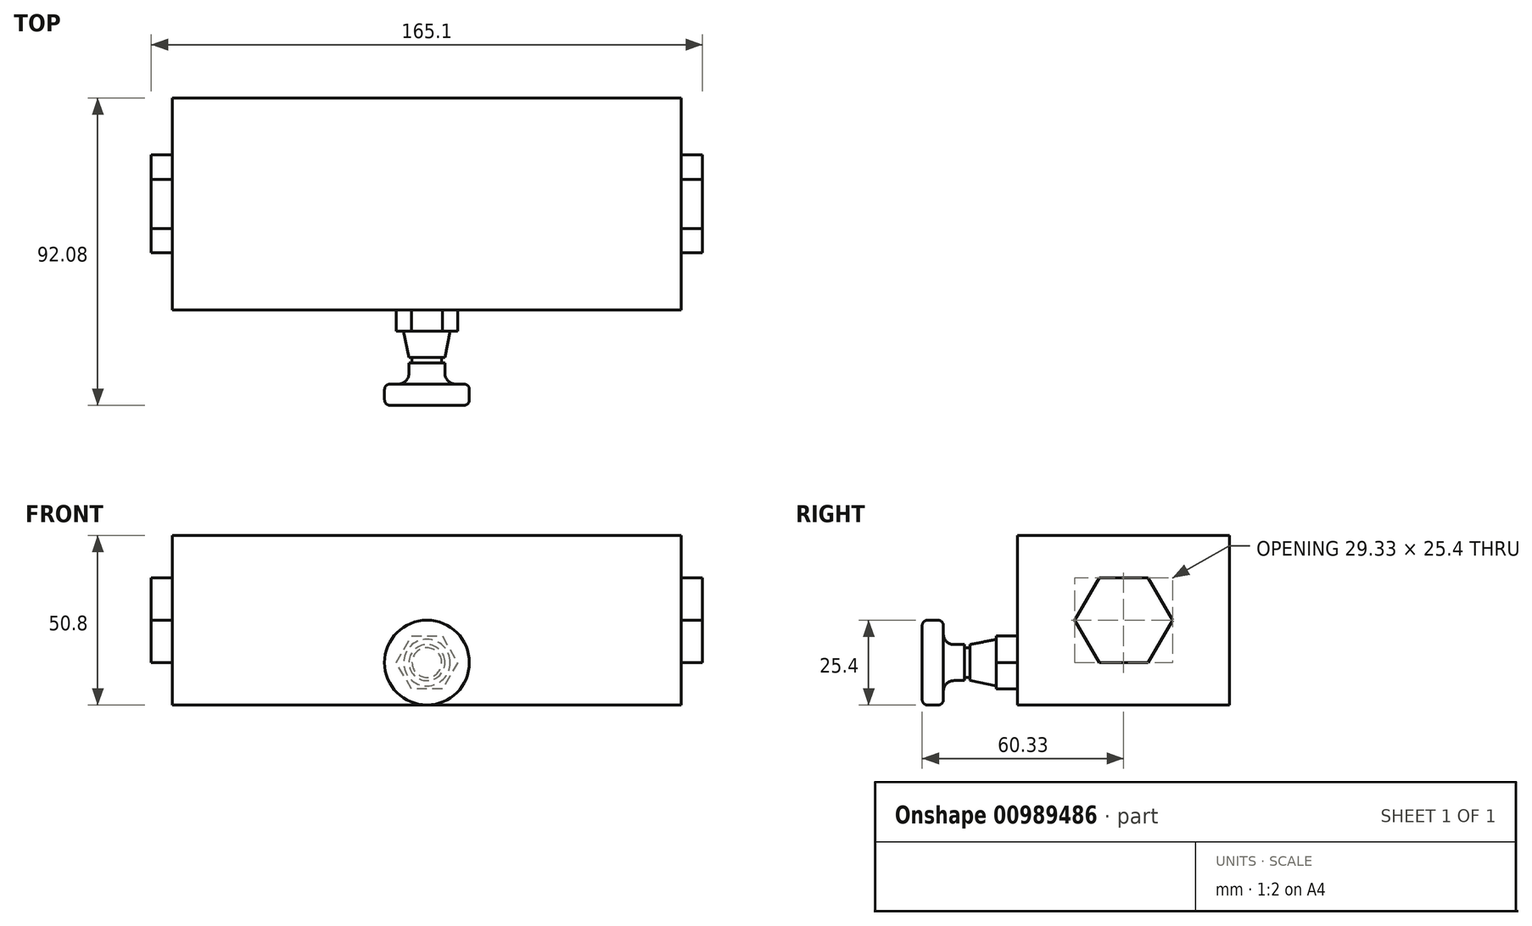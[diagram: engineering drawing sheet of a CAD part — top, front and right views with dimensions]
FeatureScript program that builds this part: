
annotation { "Feature Type Name" : "Feature", "Feature Type Description" : "" }
export const myFeature = defineFeature(function(context is Context, id is Id, definition is map)
    precondition{}
    {
        {
            var Q0;
            Q0=qCreatedBy(makeId("Right.planeOp"),FACE);
            var sketch = newSketch(context, id + "F0", { "sketchPlane" : qUnion([Q0])});
            skLineSegment(sketch, "E0.bottom", {"start": v(31.75, 25.4) * mm, "end": v(-31.75, 25.4) * mm});
            skLineSegment(sketch, "E0.top", {"start": v(31.75, -25.4) * mm, "end": v(-31.75, -25.4) * mm});
            skLineSegment(sketch, "E0.left", {"start": v(31.75, 25.4) * mm, "end": v(31.75, -25.4) * mm});
            skLineSegment(sketch, "E0.right", {"start": v(-31.75, 25.4) * mm, "end": v(-31.75, -25.4) * mm});
            skPoint(sketch, "E0.middle", {"position": v(0, 0) * mm});
            skSolve(sketch);
        }
        {
            var Q0;
            Q0 = qSketchRegion(id + "F0", true);
            extrude(context, id + "F1", {"entities" : qUnion([Q0]), "depth" : 76.2 * mm, "offsetDistance" : 25.4 * mm, "hasSecondDirection" : true, "secondDirectionOppositeDirection" : true, "secondDirectionDepth" : 76.2 * mm});
        }
        {
            var Q0;
            Q0=makeQuery(id+"F1.opExtrude","CAP_FACE",FACE,{"disambiguationData":[OSD([sQuery(id+"F0.wireOp",EDGE,"E0.bottom"),sQuery(id+"F0.wireOp",EDGE,"E0.top"),sQuery(id+"F0.wireOp",EDGE,"E0.left"),sQuery(id+"F0.wireOp",EDGE,"E0.right")])],"isStart":true});
            var sketch = newSketch(context, id + "F2", { "sketchPlane" : qUnion([Q0])});
            skCircle(sketch, "E1.cCircle", {"center": v(0, 0) * mm, "radius": 12.7 * mm, "construction": true});
            skPoint(sketch, "E1.cCircle.centerSnap0", {"position": v(0, 25.4) * mm});
            skPoint(sketch, "E1.cCircle.centerSnap1", {"position": v(31.75, 0) * mm});
            skLineSegment(sketch, "E1.0", {"start": v(-7.33, 12.7) * mm, "end": v(7.33, 12.7) * mm});
            skLineSegment(sketch, "E1.1", {"start": v(7.33, 12.7) * mm, "end": v(14.66, 0) * mm});
            skLineSegment(sketch, "E1.2", {"start": v(14.66, 0) * mm, "end": v(7.33, -12.7) * mm});
            skLineSegment(sketch, "E1.3", {"start": v(7.33, -12.7) * mm, "end": v(-7.33, -12.7) * mm});
            skLineSegment(sketch, "E1.4", {"start": v(-7.33, -12.7) * mm, "end": v(-14.66, 0) * mm});
            skLineSegment(sketch, "E1.5", {"start": v(-14.66, 0) * mm, "end": v(-7.33, 12.7) * mm});
            skPoint(sketch, "E1.0.midPoint", {"position": v(0, 12.7) * mm});
            skSolve(sketch);
        }
        {
            var Q0;
            Q0 = qSketchRegion(id + "F2", true);
            extrude(context, id + "F3", {"entities" : qUnion([Q0]), "operationType" : NewBodyOperationType.ADD, "depth" : 6.35 * mm, "offsetDistance" : 25.4 * mm});
        }
        {
            var Q0;
            Q0=qCreatedBy(makeId("Front.planeOp"),FACE);
            var sketch = newSketch(context, id + "F4", { "sketchPlane" : qUnion([Q0])});
            skLineSegment(sketch, "E2.0", {"start": v(-82.55, 12.7) * mm, "end": v(-82.55, 0) * mm, "construction": true});
            skLineSegment(sketch, "E3.0", {"start": v(-82.55, 0) * mm, "end": v(-82.55, -12.7) * mm, "construction": true});
            skLineSegment(sketch, "E4", {"start": v(-82.55, 11.11) * mm, "end": v(-98.42, 7.94) * mm});
            skLineSegment(sketch, "E5", {"start": v(-98.42, 7.94) * mm, "end": v(-98.42, 6.35) * mm});
            skLineSegment(sketch, "E6", {"start": v(-98.42, 6.35) * mm, "end": v(-100.01, 6.35) * mm});
            skLineSegment(sketch, "E7", {"start": v(-100.01, 6.35) * mm, "end": v(-100.01, 7.94) * mm});
            skLineSegment(sketch, "E8", {"start": v(-100.01, 7.94) * mm, "end": v(-103.19, 7.94) * mm});
            skLineSegment(sketch, "E9", {"start": v(-106.36, 11.11) * mm, "end": v(-106.36, 13.65) * mm});
            skLineSegment(sketch, "E10", {"start": v(-107.95, 15.24) * mm, "end": v(-112.71, 15.24) * mm});
            skLineSegment(sketch, "E11", {"start": v(-114.3, 13.65) * mm, "end": v(-114.3, 0) * mm});
            skLineSegment(sketch, "E12", {"start": v(-114.3, 0) * mm, "end": v(-82.55, 0) * mm});
            skLineSegment(sketch, "E13", {"start": v(-82.55, 0) * mm, "end": v(-82.55, 11.11) * mm});
            skPoint(sketch, "E14.visualSharp", {"position": v(-106.36, 15.24) * mm});
            skArc(sketch, "E14.filletArc", {"start": v(-106.36, 13.65) * mm, "mid": v(-106.83, 14.78) * mm, "end": v(-107.95, 15.24) * mm});
            skPoint(sketch, "E15.visualSharp", {"position": v(-114.3, 15.24) * mm});
            skArc(sketch, "E15.filletArc", {"start": v(-112.71, 15.24) * mm, "mid": v(-113.84, 14.78) * mm, "end": v(-114.3, 13.65) * mm});
            skPoint(sketch, "E16.visualSharp", {"position": v(-106.36, 7.94) * mm});
            skArc(sketch, "E16.filletArc", {"start": v(-106.36, 11.11) * mm, "mid": v(-105.43, 8.87) * mm, "end": v(-103.19, 7.94) * mm});
            skLineSegment(sketch, "E17", {"start": v(-114.3, 0) * mm, "end": v(-130.85, 0) * mm, "construction": true});
            skSolve(sketch);
        }
        {
            var Q0;
            Q0=sQuery(id+"F4.wireOp",EDGE,"E4");
            var Q1;
            Q1=sQuery(id+"F4.wireOp",EDGE,"E6");
            var Q2;
            Q2=sQuery(id+"F4.wireOp",EDGE,"E8");
            var Q3;
            Q3=sQuery(id+"F4.wireOp",EDGE,"E5");
            var Q4;
            Q4=sQuery(id+"F4.wireOp",EDGE,"E7");
            var Q5;
            Q5=sQuery(id+"F4.wireOp",EDGE,"E16.filletArc");
            var Q6;
            Q6=sQuery(id+"F4.wireOp",EDGE,"E9");
            var Q7;
            Q7=sQuery(id+"F4.wireOp",EDGE,"E14.filletArc");
            var Q8;
            Q8=sQuery(id+"F4.wireOp",EDGE,"E10");
            var Q9;
            Q9=sQuery(id+"F4.wireOp",EDGE,"E15.filletArc");
            var Q10;
            Q10=sQuery(id+"F4.wireOp",EDGE,"E11");
            var Q11;
            Q11=sQuery(id+"F4.wireOp",EDGE,"E17");
            revolve(context, id + "F5", {"bodyType" : ToolBodyType.SURFACE, "surfaceOperationType" : NewSurfaceOperationType.NEW, "surfaceEntities" : qUnion([Q0, Q1, Q2, Q3, Q4, Q5, Q6, Q7, Q8, Q9, Q10]), "axis" : qUnion([Q11]), "revolveType" : RevolveType.FULL});
        }
        {
            var Q0;
            Q0=makeQuery(id+"F5.opRevolve","SWEPT_BODY",BODY,{"disambiguationData":[OSD([sQuery(id+"F4.wireOp",EDGE,"E11")])]});
            var Q1;
            Q1=makeQuery(id+"F1.opExtrude","SWEPT_BODY",BODY,{"disambiguationData":[OSD([sQuery(id+"F0.wireOp",EDGE,"E0.bottom"),sQuery(id+"F0.wireOp",EDGE,"E0.top"),sQuery(id+"F0.wireOp",EDGE,"E0.left"),sQuery(id+"F0.wireOp",EDGE,"E0.right")])]});
            var Q2;
            Q2=qCreatedBy(makeId("Right.planeOp"),FACE);
            mirror(context, id + "F6", {"entities" : qUnion([Q0, Q1]), "mirrorPlane" : qUnion([Q2])});
        }
        {
            var Q0;
            Q0=makeQuery(id+"F1.opExtrude","SWEPT_FACE",FACE,{"disambiguationData":[OSD([sQuery(id+"F0.wireOp",EDGE,"E0.right")])]});
            var sketch = newSketch(context, id + "F7", { "sketchPlane" : qUnion([Q0])});
            skCircle(sketch, "E18.cCircle", {"center": v(0, -12.7) * mm, "radius": 7.94 * mm, "construction": true});
            skPoint(sketch, "E18.cCircle.centerSnap0", {"position": v(0, -25.4) * mm});
            skLineSegment(sketch, "E18.0", {"start": v(4.58, -4.76) * mm, "end": v(9.17, -12.7) * mm});
            skLineSegment(sketch, "E18.1", {"start": v(9.17, -12.7) * mm, "end": v(4.58, -20.64) * mm});
            skLineSegment(sketch, "E18.2", {"start": v(4.58, -20.64) * mm, "end": v(-4.58, -20.64) * mm});
            skLineSegment(sketch, "E18.3", {"start": v(-4.58, -20.64) * mm, "end": v(-9.17, -12.7) * mm});
            skLineSegment(sketch, "E18.4", {"start": v(-9.17, -12.7) * mm, "end": v(-4.58, -4.76) * mm});
            skLineSegment(sketch, "E18.5", {"start": v(-4.58, -4.76) * mm, "end": v(4.58, -4.76) * mm});
            skPoint(sketch, "E18.0.midPoint", {"position": v(6.87, -8.73) * mm});
            skLineSegment(sketch, "E19", {"start": v(0, -25.4) * mm, "end": v(0, -12.7) * mm, "construction": true});
            skSolve(sketch);
        }
        {
            var Q0;
            Q0 = qSketchRegion(id + "F7", true);
            extrude(context, id + "F8", {"entities" : qUnion([Q0]), "depth" : 6.35 * mm, "offsetDistance" : 25.4 * mm});
        }
        {
            var Q0;
            Q0=qCreatedBy(makeId("Right.planeOp"),FACE);
            var sketch = newSketch(context, id + "F9", { "sketchPlane" : qUnion([Q0])});
            skLineSegment(sketch, "E20.0", {"start": v(-38.1, -4.76) * mm, "end": v(-38.1, -12.7) * mm, "construction": true});
            skLineSegment(sketch, "E21.0", {"start": v(-38.1, -12.7) * mm, "end": v(-38.1, -20.64) * mm, "construction": true});
            skLineSegment(sketch, "E22", {"start": v(-38.1, -5.72) * mm, "end": v(-46.04, -7.3) * mm});
            skLineSegment(sketch, "E23", {"start": v(-46.04, -7.3) * mm, "end": v(-46.04, -8.26) * mm});
            skLineSegment(sketch, "E24", {"start": v(-46.04, -8.26) * mm, "end": v(-47.62, -8.26) * mm});
            skLineSegment(sketch, "E25", {"start": v(-47.62, -8.26) * mm, "end": v(-47.62, -7.3) * mm});
            skLineSegment(sketch, "E26", {"start": v(-47.62, -7.3) * mm, "end": v(-50.8, -7.3) * mm});
            skLineSegment(sketch, "E27", {"start": v(-53.98, -4.13) * mm, "end": v(-53.98, -1.59) * mm});
            skLineSegment(sketch, "E28", {"start": v(-55.56, 0) * mm, "end": v(-58.74, 0) * mm});
            skLineSegment(sketch, "E29", {"start": v(-60.33, -1.59) * mm, "end": v(-60.33, -12.7) * mm});
            skLineSegment(sketch, "E30", {"start": v(-60.33, -12.7) * mm, "end": v(-38.1, -12.7) * mm});
            skLineSegment(sketch, "E31", {"start": v(-38.1, -12.7) * mm, "end": v(-38.1, -5.72) * mm});
            skPoint(sketch, "E32.visualSharp", {"position": v(-53.98, 0) * mm});
            skArc(sketch, "E32.filletArc", {"start": v(-53.98, -1.59) * mm, "mid": v(-54.44, -0.46) * mm, "end": v(-55.56, 0) * mm});
            skPoint(sketch, "E33.visualSharp", {"position": v(-60.33, 0) * mm});
            skArc(sketch, "E33.filletArc", {"start": v(-58.74, 0) * mm, "mid": v(-59.86, -0.46) * mm, "end": v(-60.32, -1.59) * mm});
            skPoint(sketch, "E34.visualSharp", {"position": v(-53.98, -7.3) * mm});
            skArc(sketch, "E34.filletArc", {"start": v(-53.98, -4.13) * mm, "mid": v(-53.05, -6.37) * mm, "end": v(-50.8, -7.3) * mm});
            skLineSegment(sketch, "E35", {"start": v(-60.33, -12.7) * mm, "end": v(-70.57, -12.7) * mm, "construction": true});
            skSolve(sketch);
        }
        {
            var Q0;
            Q0 = qSketchRegion(id + "F9", true);
            var Q1;
            Q1=sQuery(id+"F9.wireOp",EDGE,"E35");
            revolve(context, id + "F10", {"operationType" : NewBodyOperationType.ADD, "surfaceOperationType" : NewSurfaceOperationType.NEW, "entities" : qUnion([Q0]), "axis" : qUnion([Q1]), "revolveType" : RevolveType.FULL});
        }
    });
